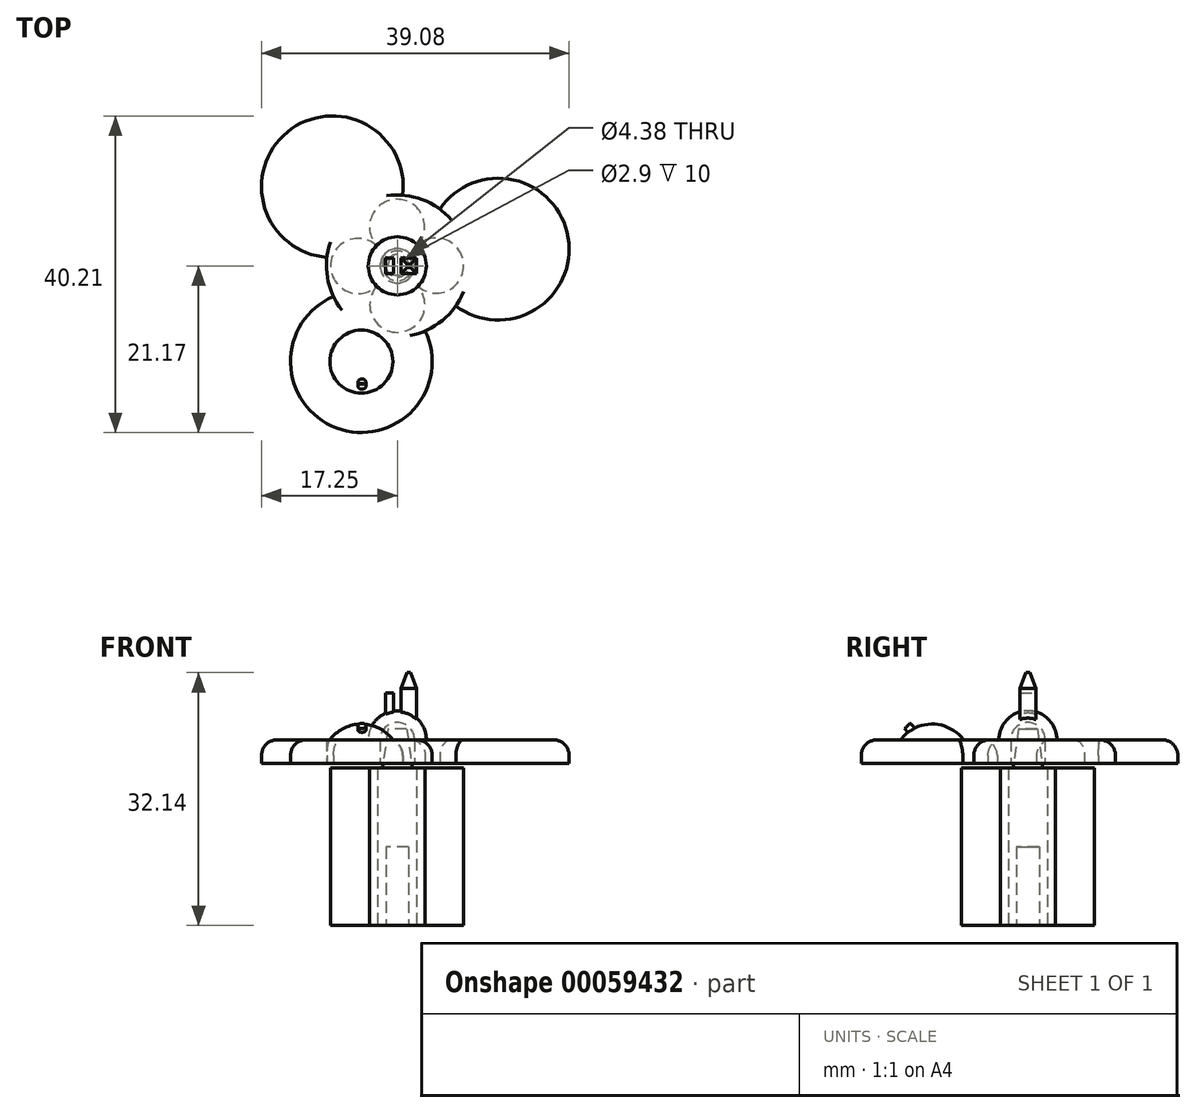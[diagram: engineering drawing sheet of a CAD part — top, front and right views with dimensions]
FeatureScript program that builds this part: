
annotation { "Feature Type Name" : "Feature", "Feature Type Description" : "" }
export const myFeature = defineFeature(function(context is Context, id is Id, definition is map)
    precondition{}
    {
        {
            var Q0;
            Q0=qCreatedBy(makeId("Top.planeOp"),FACE);
            var sketch = newSketch(context, id + "F0", { "sketchPlane" : qUnion([Q0])});
            skCircle(sketch, "E0", {"center": v(0, 0) * mm, "radius": 1.45 * mm});
            skCircle(sketch, "E1", {"center": v(0, -4.95) * mm, "radius": 3.5 * mm});
            skLineSegment(sketch, "E2", {"start": v(0, -4.95) * mm, "end": v(0, 0) * mm, "construction": true});
            skCircle(sketch, "E3.1.0", {"center": v(4.93, 0.02) * mm, "radius": 3.5 * mm});
            skCircle(sketch, "E3.2.0", {"center": v(-0.04, 4.95) * mm, "radius": 3.5 * mm});
            skPoint(sketch, "E3.center", {"position": v(-0.02, 0) * mm});
            skCircle(sketch, "E4.1.3.0", {"center": v(-4.97, -0.02) * mm, "radius": 3.5 * mm});
            skSolve(sketch);
        }
        {
            var Q0;
            Q0 = qSketchRegion(id + "F0", true);
            extrude(context, id + "F1", {"entities" : qUnion([Q0]), "depth" : 20 * mm});
        }
        {
            var Q0;
            Q0=makeQuery(id+"F1.opExtrude","CAP_FACE",FACE,{"disambiguationData":[OSD([sQuery(id+"F0.wireOp",EDGE,"E0"),sQuery(id+"F0.wireOp",EDGE,"E1"),sQuery(id+"F0.wireOp",EDGE,"E3.1.0"),sQuery(id+"F0.wireOp",EDGE,"E3.2.0"),sQuery(id+"F0.wireOp",EDGE,"E4.1.3.0")])],"isStart":false});
            var sketch = newSketch(context, id + "F2", { "sketchPlane" : qUnion([Q0])});
            skCircle(sketch, "E5.0", {"center": v(0, 0) * mm, "radius": 1.45 * mm});
            skSolve(sketch);
        }
        {
            var Q0;
            Q0 = qSketchRegion(id + "F2", true);
            extrude(context, id + "F3", {"entities" : qUnion([Q0]), "operationType" : NewBodyOperationType.ADD, "oppositeDirection" : true, "depth" : 10 * mm});
        }
        {
            var Q0;
            Q0=makeQuery(id+"F3.boolean.opBoolean","MERGE",FACE,{"derivedFrom":[makeQuery(id+"F1.opExtrude","CAP_FACE",FACE,{"disambiguationData":[OSD([sQuery(id+"F0.wireOp",EDGE,"E0"),sQuery(id+"F0.wireOp",EDGE,"E1"),sQuery(id+"F0.wireOp",EDGE,"E3.1.0"),sQuery(id+"F0.wireOp",EDGE,"E3.2.0"),sQuery(id+"F0.wireOp",EDGE,"E4.1.3.0")])],"isStart":false}),makeQuery(id+"F3.opExtrude","CAP_FACE",FACE,{"disambiguationData":[OSD([sQuery(id+"F2.wireOp",EDGE,"E5.0")])],"isStart":true})]});
            var sketch = newSketch(context, id + "F4", { "sketchPlane" : qUnion([Q0])});
            skCircle(sketch, "E6", {"center": v(0, 0) * mm, "radius": 1.9 * mm});
            skSolve(sketch);
        }
        {
            var Q0;
            Q0=makeQuery(id+"F4.imprint","IMPRINT",FACE,{"disambiguationData":[TD([[makeQuery(id+"F4.imprint","IMPRINT",EDGE,{"derivedFrom":sQuery(id+"F4.wireOp",EDGE,"E6")}),-1.0]])]});
            cPlane(context, id + "F5", {"entities" : qUnion([Q0]), "cplaneType" : CPlaneType.OFFSET, "offset" : 5 * mm, "width" : 150 * mm, "height" : 150 * mm});
        }
        {
            var Q0;
            Q0=qCreatedBy(id+"F5.planeOp",FACE);
            var sketch = newSketch(context, id + "F6", { "sketchPlane" : qUnion([Q0])});
            skCircle(sketch, "E7", {"center": v(0, 0) * mm, "radius": 1.2 * mm});
            skSolve(sketch);
        }
        {
            var Q1;
            Q1=makeQuery(id+"F6.imprint","IMPRINT",FACE,{"disambiguationData":[TD([[makeQuery(id+"F6.imprint","IMPRINT",EDGE,{"derivedFrom":sQuery(id+"F6.wireOp",EDGE,"E7")}),1.0]])]});
            var Q2;
            Q2=makeQuery(id+"F4.imprint","IMPRINT",FACE,{"disambiguationData":[TD([[makeQuery(id+"F4.imprint","IMPRINT",EDGE,{"derivedFrom":sQuery(id+"F4.wireOp",EDGE,"E6")}),1.0]])]});
            loft(context, id + "F7", {"operationType" : NewBodyOperationType.ADD, "sheetProfilesArray" : [{ "sheetProfileEntities" : qUnion([Q1]) }, { "sheetProfileEntities" : qUnion([Q2]) }]});
        }
        {
            var Q0;
            Q0=makeQuery(id+"F3.boolean.opBoolean","MERGE",FACE,{"derivedFrom":[makeQuery(id+"F1.opExtrude","CAP_FACE",FACE,{"disambiguationData":[OSD([sQuery(id+"F0.wireOp",EDGE,"E0"),sQuery(id+"F0.wireOp",EDGE,"E1"),sQuery(id+"F0.wireOp",EDGE,"E3.1.0"),sQuery(id+"F0.wireOp",EDGE,"E3.2.0"),sQuery(id+"F0.wireOp",EDGE,"E4.1.3.0")])],"isStart":false}),makeQuery(id+"F3.opExtrude","CAP_FACE",FACE,{"disambiguationData":[OSD([sQuery(id+"F2.wireOp",EDGE,"E5.0")])],"isStart":true})]});
            cPlane(context, id + "F8", {"entities" : qUnion([Q0]), "cplaneType" : CPlaneType.OFFSET, "offset" : .6 * mm, "width" : 150 * mm, "height" : 150 * mm});
        }
        {
            var Q0;
            Q0=qCreatedBy(id+"F8.planeOp",FACE);
            var sketch = newSketch(context, id + "F9", { "sketchPlane" : qUnion([Q0])});
            skCircle(sketch, "E8", {"center": v(0, 0) * mm, "radius": 9 * mm});
            skCircle(sketch, "E9.0", {"center": v(0, 0) * mm, "radius": 1.9 * mm, "construction": true});
            skCircle(sketch, "E10.0", {"center": v(0, 0) * mm, "radius": 2.2 * mm});
            skArc(sketch, "E11", {"start": v(0.68, 8.97) * mm, "mid": v(-13.97, 17) * mm, "end": v(-8.94, 1.07) * mm});
            skArc(sketch, "E12.1.0", {"start": v(-8.11, -3.9) * mm, "mid": v(-7.74, -20.6) * mm, "end": v(3.54, -8.27) * mm});
            skArc(sketch, "E12.2.0", {"start": v(7.43, -5.08) * mm, "mid": v(21.7, 3.6) * mm, "end": v(5.4, 7.2) * mm});
            skLineSegment(sketch, "E13", {"start": v(0, 0) * mm, "end": v(-8.25, 10.04) * mm, "construction": true});
            skSolve(sketch);
        }
        {
            var Q0;
            Q0 = qSketchRegion(id + "F9", true);
            extrude(context, id + "F10", {"entities" : qUnion([Q0]), "depth" : 3 * mm});
        }
        {
            var Q0;
            Q0=makeQuery(id+"F10.opExtrude","CAP_EDGE",EDGE,{"disambiguationData":[OSD([sQuery(id+"F9.wireOp",EDGE,"E12.1.0")])],"isStart":false});
            var Q1;
            Q1=makeQuery(id+"F10.opExtrude","CAP_EDGE",EDGE,{"disambiguationData":[OSD([sQuery(id+"F9.wireOp",EDGE,"E12.2.0")])],"isStart":false});
            var Q2;
            Q2=makeQuery(id+"F10.opExtrude","CAP_EDGE",EDGE,{"disambiguationData":[OSD([sQuery(id+"F9.wireOp",EDGE,"E11")])],"isStart":false});
            fillet(context, id + "F11", {"entities" : qUnion([Q0, Q1, Q2]), "radius" : 2 * mm, "tangentPropagation" : true, "allowEdgeOverflow" : false});
        }
        {
            var Q0;
            Q0=makeQuery(id+"F10.opExtrude","CAP_FACE",FACE,{"disambiguationData":[OSD([sQuery(id+"F9.wireOp",EDGE,"E8"),sQuery(id+"F9.wireOp",EDGE,"E10.0"),sQuery(id+"F9.wireOp",EDGE,"E11"),sQuery(id+"F9.wireOp",EDGE,"E12.1.0"),sQuery(id+"F9.wireOp",EDGE,"E12.2.0")])],"isStart":false});
            var sketch = newSketch(context, id + "F12", { "sketchPlane" : qUnion([Q0])});
            skCircle(sketch, "E14.0", {"center": v(0, 0) * mm, "radius": 2.2 * mm, "construction": true});
            skArc(sketch, "E15", {"start": v(0, -2.2) * mm, "mid": v(2.2, 0) * mm, "end": v(0, 2.2) * mm});
            skArc(sketch, "E16.0", {"start": v(0, -3.7) * mm, "mid": v(3.7, 0) * mm, "end": v(0, 3.7) * mm});
            skLineSegment(sketch, "E17", {"start": v(0, 3.7) * mm, "end": v(0, 2.2) * mm});
            skLineSegment(sketch, "E18", {"start": v(0, -2.2) * mm, "end": v(0, -3.7) * mm});
            skSolve(sketch);
        }
        {
            var Q0;
            Q0 = qSketchRegion(id + "F12", true);
            var Q1;
            Q1=sQuery(id+"F12.wireOp",EDGE,"E17");
            revolve(context, id + "F13", {"operationType" : NewBodyOperationType.ADD, "entities" : qUnion([Q0]), "axis" : qUnion([Q1]), "revolveType" : RevolveType.ONE_DIRECTION, "angle" : 180 * degree});
        }
        {
            var Q0;
            Q0=makeQuery(id+"F10.opExtrude","CAP_FACE",FACE,{"disambiguationData":[OSD([sQuery(id+"F9.wireOp",EDGE,"E8"),sQuery(id+"F9.wireOp",EDGE,"E10.0"),sQuery(id+"F9.wireOp",EDGE,"E11"),sQuery(id+"F9.wireOp",EDGE,"E12.1.0"),sQuery(id+"F9.wireOp",EDGE,"E12.2.0")])],"isStart":true});
            var sketch = newSketch(context, id + "F14", { "sketchPlane" : qUnion([Q0])});
            skLineSegment(sketch, "E19", {"start": v(0, 0) * mm, "end": v(-4.57, 12.17) * mm, "construction": true});
            skLineSegment(sketch, "E20", {"start": v(-4.57, 12.17) * mm, "end": v(-6.33, 16.85) * mm, "construction": true});
            skArc(sketch, "E21", {"start": v(-2.81, 7.49) * mm, "mid": v(0.1, 13.93) * mm, "end": v(-6.33, 16.85) * mm});
            skLineSegment(sketch, "E22", {"start": v(-6.33, 16.85) * mm, "end": v(-2.81, 7.49) * mm});
            skPoint(sketch, "E23.center", {"position": v(-0.34, -2.03) * mm});
            skSolve(sketch);
        }
        {
            var Q0;
            Q0=makeQuery(id+"F14.imprint","IMPRINT",FACE,{"disambiguationData":[TD([[makeQuery(id+"F14.imprint","IMPRINT",EDGE,{"derivedFrom":sQuery(id+"F14.wireOp",EDGE,"E21")}),1.0]])]});
            var Q1;
            Q1=sQuery(id+"F14.wireOp",EDGE,"E22");
            revolve(context, id + "F15", {"operationType" : NewBodyOperationType.ADD, "entities" : qUnion([Q0]), "axis" : qUnion([Q1]), "revolveType" : RevolveType.ONE_DIRECTION, "oppositeDirection" : true, "angle" : 180 * degree});
        }
        {
            var Q0;
            Q0=qCreatedBy(makeId("Front.planeOp"),FACE);
            var sketch = newSketch(context, id + "F16", { "sketchPlane" : qUnion([Q0])});
            skLineSegment(sketch, "E24", {"start": v(0, 0) * mm, "end": v(0, 27.3) * mm, "construction": true});
            skArc(sketch, "E25", {"start": v(3.7, 23.6) * mm, "mid": v(0, 27.3) * mm, "end": v(-3.7, 23.6) * mm, "construction": true});
            skLineSegment(sketch, "E26.bottom", {"start": v(-1.48, 26.58) * mm, "end": v(-0.48, 26.58) * mm});
            skLineSegment(sketch, "E26.top", {"start": v(-1.48, 29.58) * mm, "end": v(-0.48, 29.58) * mm});
            skLineSegment(sketch, "E26.left", {"start": v(-1.48, 26.58) * mm, "end": v(-1.48, 29.58) * mm});
            skLineSegment(sketch, "E26.right", {"start": v(-0.48, 26.58) * mm, "end": v(-0.48, 29.58) * mm});
            skLineSegment(sketch, "E27.bottom", {"start": v(2.45, 26.14) * mm, "end": v(0.45, 26.14) * mm});
            skLineSegment(sketch, "E27.top", {"start": v(2.45, 30.14) * mm, "end": v(0.45, 30.14) * mm});
            skLineSegment(sketch, "E27.left", {"start": v(2.45, 26.14) * mm, "end": v(2.45, 30.14) * mm});
            skLineSegment(sketch, "E27.right", {"start": v(0.45, 26.14) * mm, "end": v(0.45, 30.14) * mm});
            skArc(sketch, "E28", {"start": v(2.2, 23.6) * mm, "mid": v(0, 25.8) * mm, "end": v(-2.2, 23.6) * mm, "construction": true});
            skSolve(sketch);
        }
        {
            var Q0;
            Q0 = qSketchRegion(id + "F16", true);
            extrude(context, id + "F17", {"entities" : qUnion([Q0]), "operationType" : NewBodyOperationType.ADD, "endBound" : BoundingType.SYMMETRIC, "depth" : 2 * mm, "hasSecondDirection" : true, "secondDirectionOppositeDirection" : true, "secondDirectionDepth" : 25 * mm});
        }
        {
            var Q0;
            Q0=makeQuery(id+"F17.opExtrude","SWEPT_FACE",FACE,{"disambiguationData":[OSD([sQuery(id+"F16.wireOp",EDGE,"E27.top")])]});
            cPlane(context, id + "F18", {"entities" : qUnion([Q0]), "cplaneType" : CPlaneType.OFFSET, "offset" : 2 * mm, "width" : 150 * mm, "height" : 150 * mm});
        }
        {
            var Q0;
            Q0=qCreatedBy(id+"F18.planeOp",FACE);
            var sketch = newSketch(context, id + "F19", { "sketchPlane" : qUnion([Q0])});
            skLineSegment(sketch, "E29.0.0", {"start": v(2.45, 1) * mm, "end": v(0.45, 1) * mm, "construction": true});
            skLineSegment(sketch, "E29.0.1", {"start": v(0.45, 1) * mm, "end": v(0.45, -1) * mm, "construction": true});
            skLineSegment(sketch, "E29.0.2", {"start": v(0.45, -1) * mm, "end": v(2.45, -1) * mm, "construction": true});
            skLineSegment(sketch, "E29.0.3", {"start": v(2.45, -1) * mm, "end": v(2.45, 1) * mm, "construction": true});
            skLineSegment(sketch, "E30", {"start": v(0.45, 1) * mm, "end": v(2.45, -1) * mm, "construction": true});
            skLineSegment(sketch, "E31.rect.bottom", {"start": v(1.7, -0.25) * mm, "end": v(1.2, -0.25) * mm});
            skLineSegment(sketch, "E31.rect.top", {"start": v(1.7, 0.25) * mm, "end": v(1.2, 0.25) * mm});
            skLineSegment(sketch, "E31.rect.left", {"start": v(1.7, -0.25) * mm, "end": v(1.7, 0.25) * mm});
            skLineSegment(sketch, "E31.rect.right", {"start": v(1.2, -0.25) * mm, "end": v(1.2, 0.25) * mm});
            skPoint(sketch, "E31.rect.middle", {"position": v(1.45, 0) * mm});
            skSolve(sketch);
        }
        {
            var Q1;
            Q1=makeQuery(id+"F17.opExtrude","SWEPT_FACE",FACE,{"disambiguationData":[OSD([sQuery(id+"F16.wireOp",EDGE,"E27.top")])]});
            var Q2;
            Q2=makeQuery(id+"F19.imprint","IMPRINT",FACE,{"disambiguationData":[TD([[makeQuery(id+"F19.imprint","IMPRINT",EDGE,{"derivedFrom":sQuery(id+"F19.wireOp",EDGE,"E31.rect.bottom")}),-1.0]])]});
            loft(context, id + "F20", {"operationType" : NewBodyOperationType.ADD, "sheetProfilesArray" : [{ "sheetProfileEntities" : qUnion([Q1]) }, { "sheetProfileEntities" : qUnion([Q2]) }]});
        }
        {
            var Q0;
            Q0=qCreatedBy(makeId("Right.planeOp"),FACE);
            cPlane(context, id + "F21", {"entities" : qUnion([Q0]), "cplaneType" : CPlaneType.OFFSET, "offset" : 4.5 * mm, "oppositeDirection" : true, "width" : 150 * mm, "height" : 150 * mm});
        }
        {
            var Q0;
            Q0=qCreatedBy(id+"F21.planeOp",FACE);
            var sketch = newSketch(context, id + "F22", { "sketchPlane" : qUnion([Q0])});
            skLineSegment(sketch, "E32.0", {"start": v(-14.94, 25.7) * mm, "end": v(-13.91, 24.61) * mm});
            skLineSegment(sketch, "E33.0", {"start": v(-15.3, 25.36) * mm, "end": v(-14.94, 25.7) * mm});
            skLineSegment(sketch, "E33.1", {"start": v(-14.28, 24.27) * mm, "end": v(-15.3, 25.36) * mm});
            skLineSegment(sketch, "E33.2", {"start": v(-13.91, 24.61) * mm, "end": v(-14.28, 24.27) * mm});
            skSolve(sketch);
        }
        {
            var Q0;
            Q0=makeQuery(id+"F22.imprint","IMPRINT",FACE,{"disambiguationData":[TD([[makeQuery(id+"F22.imprint","IMPRINT",EDGE,{"derivedFrom":sQuery(id+"F22.wireOp",EDGE,"E32.0")}),-1.0]])]});
            var Q1;
            Q1=sQuery(id+"F22.wireOp",EDGE,"E33.1");
            revolve(context, id + "F23", {"operationType" : NewBodyOperationType.ADD, "entities" : qUnion([Q0]), "axis" : qUnion([Q1]), "revolveType" : RevolveType.FULL});
        }
        {
            var Q0;
            Q0=makeQuery(id+"F1.opExtrude","SWEPT_BODY",BODY,{"disambiguationData":[OSD([sQuery(id+"F0.wireOp",EDGE,"E0"),sQuery(id+"F0.wireOp",EDGE,"E1"),sQuery(id+"F0.wireOp",EDGE,"E3.1.0"),sQuery(id+"F0.wireOp",EDGE,"E3.2.0"),sQuery(id+"F0.wireOp",EDGE,"E4.1.3.0")])]});
            var Q1;
            Q1=makeQuery(id+"F10.opExtrude","SWEPT_BODY",BODY,{"disambiguationData":[OSD([sQuery(id+"F9.wireOp",EDGE,"E8"),sQuery(id+"F9.wireOp",EDGE,"E10.0"),sQuery(id+"F9.wireOp",EDGE,"E11"),sQuery(id+"F9.wireOp",EDGE,"E12.1.0"),sQuery(id+"F9.wireOp",EDGE,"E12.2.0")])]});
            transform(context, id + "F24", {"entities" : qUnion([Q0, Q1]), "transformType" : TransformType.TRANSLATION_3D, "dx" : 0 * mm, "dy" : 25 * mm, "dz" : 0 * mm, "makeCopy" : false});
        }
    });
